# Revit family: Basketball_Backstop-Wall_Mount-Stationary-IPIbyBison-IP10WB
name_source: partatom
category: Specialty Equipment
units: mm (PartAtom-declared; Revit-internal decimal feet)

## family parameters
Always vertical = No
Cut with Voids When Loaded = No
Enable Cutting in Views = No
Maintain Annotation Orientation = No
OmniClass Number = 23.40.50.34.14
OmniClass Title = Gymnasium Equipment
Part Type = Normal
Room Calculation Point = No
Round Connector Dimension = Use Diameter
Shared = No
Work Plane-Based = Yes

## types (1)
- Wall Mounted Stationary
    CAD Details = https://www.arcat.com
    Default Elevation = 0' - 0"
    Description = Basketball Frame and Backboard, Wall Mount
    Keynote = 11 66 00
    Manufacturer = IPI by Bison
    Model = IP10WB
    Product Page URL = https://www.arcat.com
    Specification = https://www.arcat.com
    URL = https://ipibybison.com
    Unit Depth = 2' - 8"
    Unit Width = 7' - 0"
    Wall Plate Material = Wood - IPI by Bison
    wall distance text = 1 to 10 ft from Wall

## geometry (parser evidence)
native form markers: Sweep x4
no freeform markers — native parametric forms only
